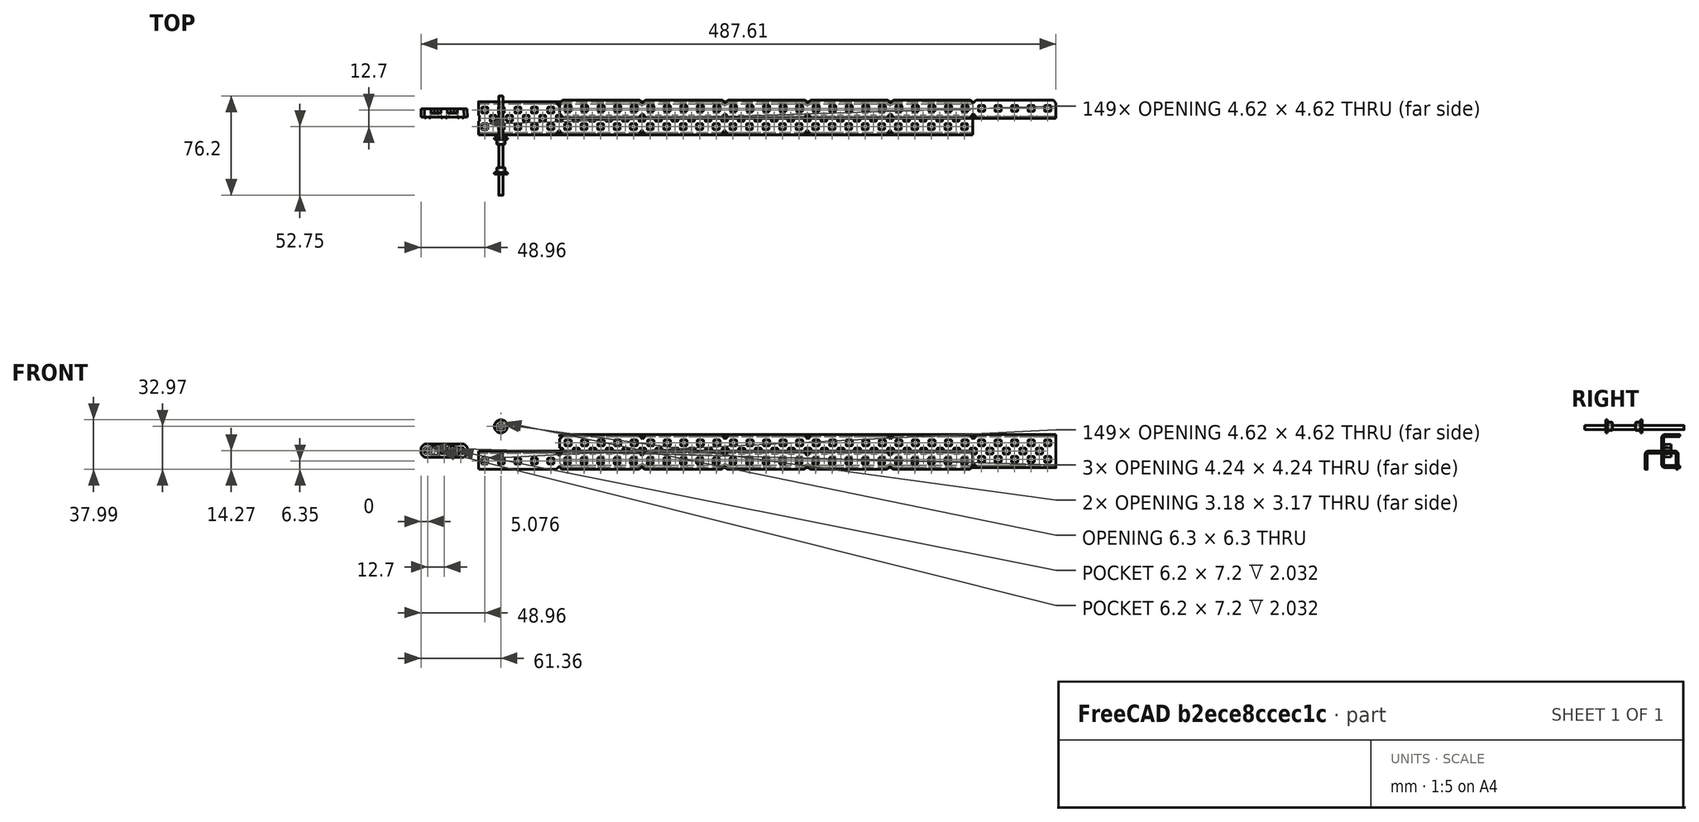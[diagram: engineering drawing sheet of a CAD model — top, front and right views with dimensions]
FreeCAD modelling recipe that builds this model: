
FCSTD DOCUMENT  (FreeCAD 0.19R24267 +148 (Git))
Label: Vex cad
License: All rights reserved
LicenseURL: http://en.wikipedia.org/wiki/All_rights_reserved
objects: Part::Feature×6, PartDesign::FeatureBase×1, Sketcher::SketchObject×1, PartDesign::Pocket×1, PartDesign::Body×1, Part::Box×1, Part::Cut×1
note: 13 computed .brp shape members not serialized (recipe doc carries the construction recipe); baked Part::Feature solids carry a one-line shape summary decoded from their .brp

FEATURE [Part::Feature] Part__Feature  label="276-2250-005 Rev1"
  Placement = pos=(-140,-43,19) rot=(0,0,1;0rad)
  shape: bbox 10.03 x 5.08 x 10.03 mm, 29 faces (baked)
FEATURE [Part::Feature] Part__Feature001  label="276-2250-005 Rev002"
  Placement = pos=(-140,-15,19) rot=(0,0,1;3.14159rad)
  shape: bbox 10.03 x 5.08 x 10.03 mm, 29 faces (baked)
FEATURE [Part::Feature] Part__Feature003  label="SHAFT-3000"
  Placement = pos=(-140,-21,18) rot=(-1,0,0;1.5708rad)
  shape: bbox 4.774 x 76.2 x 4.774 mm, 18 faces (baked)
FEATURE [Part::Feature] Part__Feature004  label="BEARING-FLAT"
  Placement = pos=(-210,90,13) rot=(0,0,1;4.71239rad)
  shape: bbox 35.56 x 7.043 x 10.16 mm, 134 faces (baked)
FEATURE [Part::Feature] Solid001  label="276-2289-001 Rev002"
  Placement = pos=(64,0,0) rot=(1,0,0;1.5708rad)
  shape: bbox 444.5 x 13.97 x 25.4 mm, 1618 faces (baked)
FEATURE [PartDesign::FeatureBase] BaseFeature
  BaseFeature = -> Solid001
FEATURE [Part::Feature] Solid002  label="276-2289-001 Rev003"
  Placement = pos=(64,0,0) rot=(1,0,0;1.5708rad)
  shape: bbox 444.5 x 13.97 x 25.4 mm, 1618 faces (baked)
FEATURE [Sketcher::SketchObject] Sketch
  FullyConstrained = false
  MapMode = 5
  Placement = pos=(-222.25,-1.4e-13,0) rot=(0.57735,-0.57735,-0.57735;2.0944rad)
  Support = -> [BaseFeature]
  sketch-geometry (4):
    g0: LineSegment StartX=20 StartY=-20 StartZ=0 EndX=-20 EndY=-20 EndZ=0
    g1: LineSegment StartX=-20 StartY=-20 StartZ=0 EndX=-20 EndY=10 EndZ=0
    g2: LineSegment StartX=-20 StartY=10 StartZ=0 EndX=20 EndY=10 EndZ=0
    g3: LineSegment StartX=20 StartY=10 StartZ=0 EndX=20 EndY=-20 EndZ=0
  constraints (8):
    c: Coincident(g0,g1)
    c: Coincident(g1,g2)
    c: Coincident(g2,g3)
    c: Coincident(g3,g0)
    c: Horizontal(g0)
    c: Horizontal(g2)
    c: Vertical(g1)
    c: Vertical(g3)
FEATURE [PartDesign::Pocket] Pocket
  BaseFeature = -> BaseFeature
  Length = 65
  Length2 = 100
  Profile = -> Sketch
  Type = 0
FEATURE [PartDesign::Body] Body  label="1x2x30"
  BaseFeature = -> Solid001
  Group = -> [BaseFeature,Sketch,Pocket]
  Origin = -> Origin
  Tip = -> Pocket
FEATURE [Part::Box] Box  label="Cube"
  AttacherType = Attacher::AttachEngine3D
  Height = 30
  Length = 86
  Placement = pos=(-181,-4,-16) rot=(0,0,1;0rad)
  Width = 20
FEATURE [Part::Cut] Cut
  Base = -> Solid002
  Tool = -> Box
